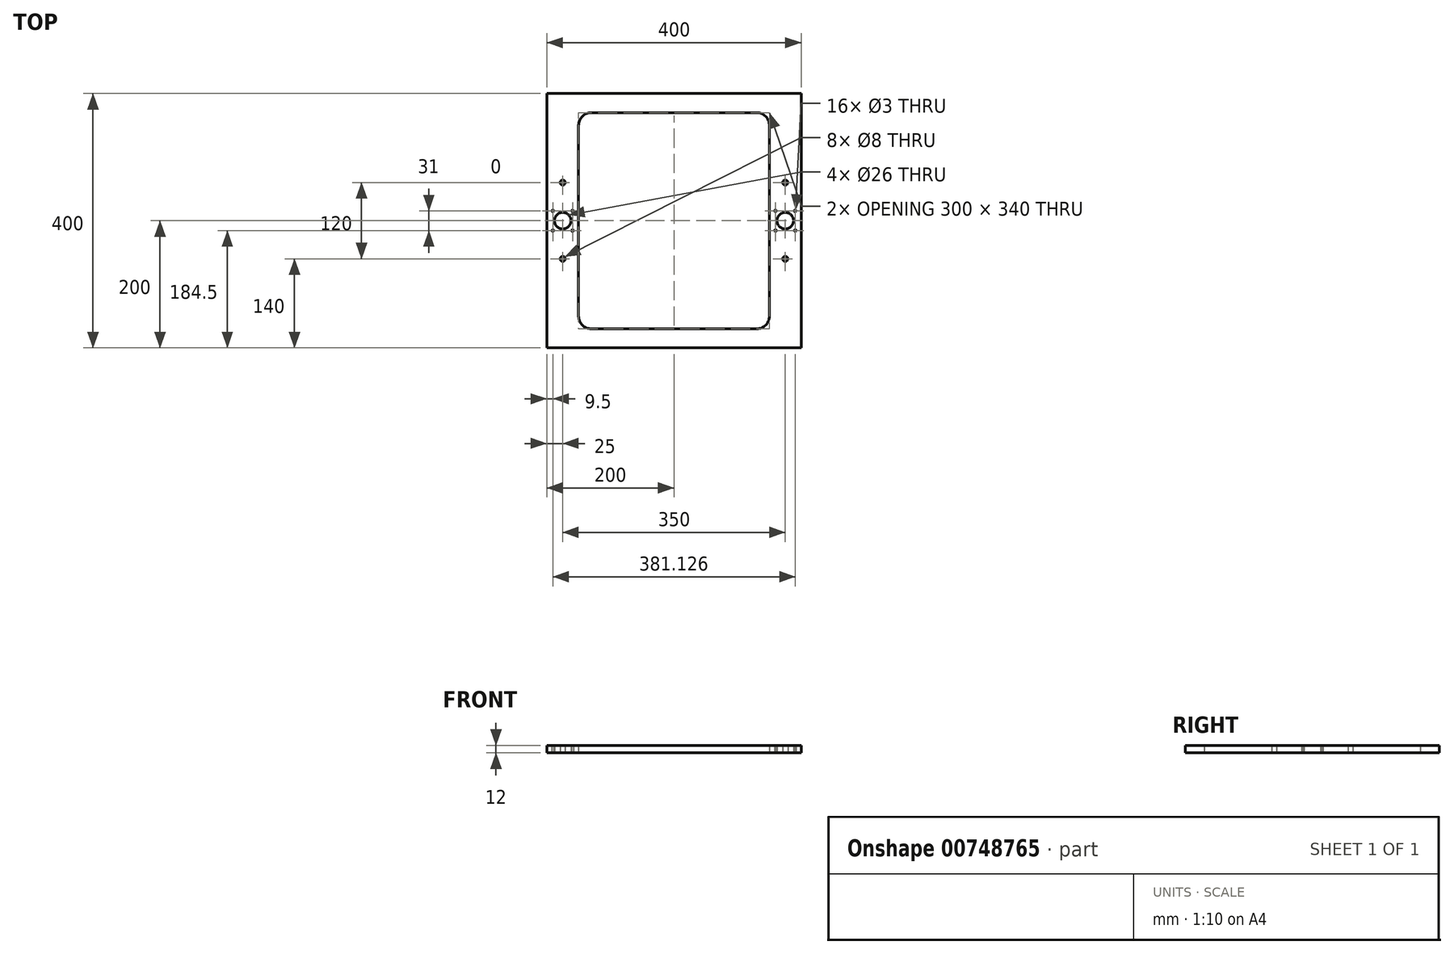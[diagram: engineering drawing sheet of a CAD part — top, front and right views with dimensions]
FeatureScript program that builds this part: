
annotation { "Feature Type Name" : "Feature", "Feature Type Description" : "" }
export const myFeature = defineFeature(function(context is Context, id is Id, definition is map)
    precondition{}
    {
        {
            var Q0;
            Q0=qCreatedBy(makeId("Top.planeOp"),FACE);
            var sketch = newSketch(context, id + "F0", { "sketchPlane" : qUnion([Q0])});
            skLineSegment(sketch, "E0.bottom", {"start": v(200, 200) * mm, "end": v(-200, 200) * mm});
            skLineSegment(sketch, "E0.top", {"start": v(200, -200) * mm, "end": v(-200, -200) * mm});
            skLineSegment(sketch, "E0.left", {"start": v(200, 200) * mm, "end": v(200, -200) * mm});
            skLineSegment(sketch, "E0.right", {"start": v(-200, 200) * mm, "end": v(-200, -200) * mm});
            skPoint(sketch, "E0.middle", {"position": v(0, 0) * mm});
            skCircle(sketch, "E1", {"center": v(-175, 0) * mm, "radius": 13 * mm});
            skCircle(sketch, "E2", {"center": v(175, 0) * mm, "radius": 13 * mm});
            skCircle(sketch, "E3", {"center": v(159.5, 15.5) * mm, "radius": 1.5 * mm});
            skCircle(sketch, "E4", {"center": v(190.5, 15.5) * mm, "radius": 1.5 * mm});
            skCircle(sketch, "E5", {"center": v(190.63, -15.5) * mm, "radius": 1.5 * mm});
            skCircle(sketch, "E6", {"center": v(159.63, -15.5) * mm, "radius": 1.5 * mm});
            skCircle(sketch, "E7", {"center": v(-190.5, 15.5) * mm, "radius": 1.5 * mm});
            skCircle(sketch, "E8", {"center": v(-159.5, 15.5) * mm, "radius": 1.5 * mm});
            skCircle(sketch, "E9", {"center": v(-159.5, -15.5) * mm, "radius": 1.5 * mm});
            skCircle(sketch, "E10", {"center": v(-190.5, -15.5) * mm, "radius": 1.5 * mm});
            skLineSegment(sketch, "E11.bottom", {"start": v(130, 170) * mm, "end": v(-130, 170) * mm});
            skLineSegment(sketch, "E11.top", {"start": v(130, -170) * mm, "end": v(-130, -170) * mm});
            skLineSegment(sketch, "E11.left", {"start": v(150, 150) * mm, "end": v(150, -150) * mm});
            skLineSegment(sketch, "E11.right", {"start": v(-150, 150) * mm, "end": v(-150, -150) * mm});
            skPoint(sketch, "E12.visualSharp", {"position": v(-150, 170) * mm});
            skArc(sketch, "E12.filletArc", {"start": v(-130, 170) * mm, "mid": v(-144.14, 164.14) * mm, "end": v(-150, 150) * mm});
            skPoint(sketch, "E13.visualSharp", {"position": v(150, 170) * mm});
            skArc(sketch, "E13.filletArc", {"start": v(150, 150) * mm, "mid": v(144.14, 164.14) * mm, "end": v(130, 170) * mm});
            skPoint(sketch, "E14.visualSharp", {"position": v(150, -170) * mm});
            skArc(sketch, "E14.filletArc", {"start": v(130, -170) * mm, "mid": v(144.14, -164.14) * mm, "end": v(150, -150) * mm});
            skPoint(sketch, "E15.visualSharp", {"position": v(-150, -170) * mm});
            skArc(sketch, "E15.filletArc", {"start": v(-150, -150) * mm, "mid": v(-144.14, -164.14) * mm, "end": v(-130, -170) * mm});
            skCircle(sketch, "E16", {"center": v(175, 60) * mm, "radius": 4 * mm});
            skCircle(sketch, "E17", {"center": v(175, -60) * mm, "radius": 4 * mm});
            skCircle(sketch, "E18", {"center": v(-175, 60) * mm, "radius": 4 * mm});
            skCircle(sketch, "E19", {"center": v(-175, -60) * mm, "radius": 4 * mm});
            skSolve(sketch);
        }
        {
            var Q0;
            Q0=qSketchRegion(id+"F0",true);
            extrude(context, id + "F1", {"entities" : qUnion([Q0]), "depth" : 12 * mm, "offsetDistance" : 25 * mm});
        }
    });
